# Revit family: ledspot3c-c-cs_10w-930_940_950-36d-wh_541001187400_ab47
name_source: partatom
category: Lighting Fixtures
units: mm (PartAtom-declared; Revit-internal decimal feet)

## family parameters
Cut with Voids When Loaded = No
Host = Face
Light Source = No
Part Type = Normal
Room Calculation Point = No
Round Connector Dimension = Use Diameter
Shared = No

## types (1)
- LEDSpot3C-C-CS 10W-930/940/950-36D-WH (1 x LED, 1000 lm, 3000)
    Apparent Load = 10 VA
    Approval mark = ENEC, CE
    CIE Flux Codes = 94 99 100 100 100
    Color Rendering = 90
    Color Temperature = 3000
    Control Gear = Electronic ballast
    Default Elevation = 1800 mm
    Description = High performance compact track spot with high luminous efficiency and homogeneous light distribution. Various beam angles achievable with exchangeable reflectors. Fitting common Global/Nordic Aluminum® 3C Tracks – and many other standard types.
    Frequency = 60 Hz
    Height = 70 mm
    Lamp = 1 x LED
    Lamp Light Flux = 1000 lm
    Lamp count = 1
    Length = 227 mm
    Luminous efficacy = 100 lm/W
    Manufacturer = OPPLE
    ModVariant = No
    Model = 541001187400
    Number of Poles = 1
    OnlyDefault = Yes
    Power Factor = 1
    Product Name = LEDSpot3C-C-CS 10W-930/940/950-36D-WH
    Product group = Track mounted spotlight
    ProductGroupID = 12
    Protection Class = Protection class I
    Protection Degree = IP 20
    RLX_Detail_Level = 1
    RlxData = <blob elided: 46493 chars, md5=834e6cf4>
    Socket = socket
    Standby Power = 0 W
    System Light Flux = 1000 lm
    System Power = 10 W
    Type Comments = Product without accessories
    Type Image = web_pf_3cc_cs_10w_wh.jpg
    URL = http://relux.com
    VarID = ---
    Voltage = 230 V
    Voltage Range = 220-240 V
    Weight = 0.00 kg
    Width = 47 mm

## geometry (parser evidence)
native form markers: Sweep x15
no freeform markers — native parametric forms only
